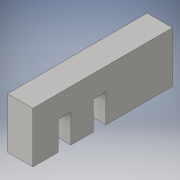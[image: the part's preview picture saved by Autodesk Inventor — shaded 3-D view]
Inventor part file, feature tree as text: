
AUTODESK INVENTOR PART (.ipt)
format: ipt  version: 2016 (Build 200138000, 138)  size: 104,960 bytes
history: native  units: in
note: dims shown in document units (in); Inventor stores cm internally (conversion verified against a paired STEP export)
features: extrude x2, sketch x2
ambient origin geometry x8: Origin, YZ Plane, XZ Plane, XY Plane, X Axis, Y Axis, Z Axis, Center Point
bodies: Solid1 (feature_tree)
feature tree (4):
  extrude  "Extrusion1"  Depth=4.0in
  extrude  "Extrusion2"  Depth=1.0in
  sketch  "Sketch1"  dims[d0=2.0in d1=4.0in]
  sketch  "Sketch2"  dims[d2=11.0in d3=0.0in d4=1.0in d5=2.25in d6=2.0in d7=1.0in d8=1.75in d9=10.5in d10=0.0in]
